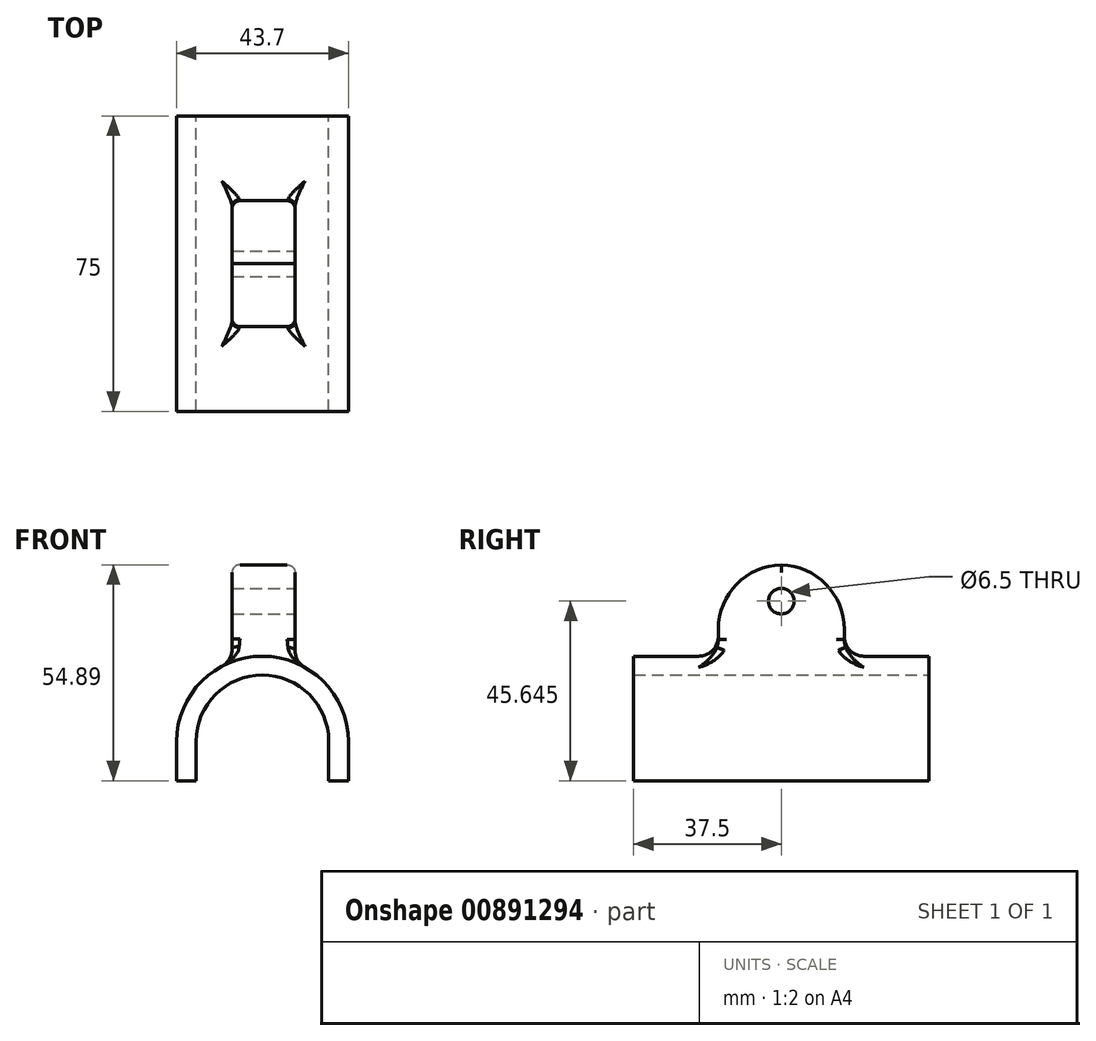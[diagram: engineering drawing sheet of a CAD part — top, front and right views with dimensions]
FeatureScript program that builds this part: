
annotation { "Feature Type Name" : "Feature", "Feature Type Description" : "" }
export const myFeature = defineFeature(function(context is Context, id is Id, definition is map)
    precondition{}
    {
        {
            var Q0;
            Q0=qCreatedBy(makeId("Front.planeOp"),FACE);
            var sketch = newSketch(context, id + "F0", { "sketchPlane" : qUnion([Q0])});
            skArc(sketch, "E0", {"start": v(16.56, 0) * mm, "mid": v(-0.29, 16.85) * mm, "end": v(-17.14, 0) * mm});
            skLineSegment(sketch, "E1", {"start": v(-17.14, 0) * mm, "end": v(-22.14, 0) * mm});
            skLineSegment(sketch, "E2", {"start": v(16.56, 0) * mm, "end": v(21.56, 0) * mm});
            skArc(sketch, "E3", {"start": v(21.56, 0) * mm, "mid": v(-0.29, 21.66) * mm, "end": v(-22.14, 0) * mm});
            skSolve(sketch);
        }
        {
            var Q0;
            Q0=makeQuery(id+"F0.imprint","IMPRINT",FACE,{"disambiguationData":[TD([[makeQuery(id+"F0.imprint","IMPRINT",EDGE,{"derivedFrom":sQuery(id+"F0.wireOp",EDGE,"E0")}),-1.0]])]});
            extrude(context, id + "F1", {"entities" : qUnion([Q0]), "endBound" : BoundingType.SYMMETRIC, "depth" : 75 * mm, "offsetDistance" : 25 * mm});
        }
        {
            var Q0;
            Q0=qCreatedBy(makeId("Top.planeOp"),FACE);
            cPlane(context, id + "F2", {"entities" : qUnion([Q0]), "cplaneType" : CPlaneType.OFFSET, "offset" : 19.9 * mm, "width" : 150 * mm, "height" : 150 * mm});
        }
        {
            var Q0;
            Q0=qCreatedBy(id+"F2.planeOp",FACE);
            var sketch = newSketch(context, id + "F3", { "sketchPlane" : qUnion([Q0])});
            skLineSegment(sketch, "E4.bottom", {"start": v(-8, 16) * mm, "end": v(8, 16) * mm});
            skLineSegment(sketch, "E4.top", {"start": v(-8, -16) * mm, "end": v(8, -16) * mm});
            skLineSegment(sketch, "E4.left", {"start": v(-8, 16) * mm, "end": v(-8, -16) * mm});
            skLineSegment(sketch, "E4.right", {"start": v(8, 16) * mm, "end": v(8, -16) * mm});
            skPoint(sketch, "E4.middle", {"position": v(0, 0) * mm});
            skSolve(sketch);
        }
        {
            var Q0;
            Q0 = qSketchRegion(id + "F3", true);
            extrude(context, id + "F4", {"entities" : qUnion([Q0]), "operationType" : NewBodyOperationType.ADD, "depth" : 25 * mm, "offsetDistance" : 25 * mm});
        }
        {
            var Q0;
            Q0=makeQuery(id+"F4.boolean.opBoolean","INTERSECT",EDGE,{"derivedFrom":[makeQuery(id+"F1.opExtrude","SWEPT_FACE",FACE,{"disambiguationData":[OSD([sQuery(id+"F0.wireOp",EDGE,"E3")])]}),makeQuery(id+"F4.opExtrude","SWEPT_FACE",FACE,{"disambiguationData":[OSD([sQuery(id+"F3.wireOp",EDGE,"E4.right")])]})]});
            var Q1;
            Q1=makeQuery(id+"F4.boolean.opBoolean","INTERSECT",EDGE,{"derivedFrom":[makeQuery(id+"F1.opExtrude","SWEPT_FACE",FACE,{"disambiguationData":[OSD([sQuery(id+"F0.wireOp",EDGE,"E3")])]}),makeQuery(id+"F4.opExtrude","SWEPT_FACE",FACE,{"disambiguationData":[OSD([sQuery(id+"F3.wireOp",EDGE,"E4.left")])]})]});
            fillet(context, id + "F5", {"entities" : qUnion([Q0, Q1]), "radius" : 5 * mm, "tangentPropagation" : true, "allowEdgeOverflow" : false});
        }
        {
            var Q0;
            Q0=makeQuery(id+"F4.boolean.opBoolean","INTERSECT",EDGE,{"derivedFrom":[makeQuery(id+"F1.opExtrude","SWEPT_FACE",FACE,{"disambiguationData":[OSD([sQuery(id+"F0.wireOp",EDGE,"E3")])]}),makeQuery(id+"F4.opExtrude","SWEPT_FACE",FACE,{"disambiguationData":[OSD([sQuery(id+"F3.wireOp",EDGE,"E4.top")])]})]});
            var Q1;
            Q1=makeQuery(id+"F4.boolean.opBoolean","INTERSECT",EDGE,{"derivedFrom":[makeQuery(id+"F1.opExtrude","SWEPT_FACE",FACE,{"disambiguationData":[OSD([sQuery(id+"F0.wireOp",EDGE,"E3")])]}),makeQuery(id+"F4.opExtrude","SWEPT_FACE",FACE,{"disambiguationData":[OSD([sQuery(id+"F3.wireOp",EDGE,"E4.bottom")])]})]});
            fillet(context, id + "F6", {"entities" : qUnion([Q0, Q1]), "radius" : 5 * mm, "tangentPropagation" : true, "allowEdgeOverflow" : false});
        }
        {
            var Q0;
            Q0=makeQuery(id+"F4.opExtrude","CAP_EDGE",EDGE,{"disambiguationData":[OSD([sQuery(id+"F3.wireOp",EDGE,"E4.top")])],"isStart":false});
            var Q1;
            Q1=makeQuery(id+"F4.opExtrude","CAP_EDGE",EDGE,{"disambiguationData":[OSD([sQuery(id+"F3.wireOp",EDGE,"E4.bottom")])],"isStart":false});
            fillet(context, id + "F7", {"entities" : qUnion([Q0, Q1]), "radius" : 16.42 * mm, "tangentPropagation" : true, "allowEdgeOverflow" : false});
        }
        {
            var Q0;
            Q0=makeQuery(id+"F4.opExtrude","SWEPT_FACE",FACE,{"disambiguationData":[OSD([sQuery(id+"F3.wireOp",EDGE,"E4.right")])]});
            var sketch = newSketch(context, id + "F8", { "sketchPlane" : qUnion([Q0])});
            skCircle(sketch, "E5", {"center": v(0, 35.64) * mm, "radius": 3.25 * mm});
            skSolve(sketch);
        }
        {
            var Q0;
            Q0 = qSketchRegion(id + "F8", true);
            extrude(context, id + "F9", {"entities" : qUnion([Q0]), "operationType" : NewBodyOperationType.REMOVE, "oppositeDirection" : true, "depth" : 25 * mm, "offsetDistance" : 25 * mm});
        }
        {
            var Q0;
            Q0=makeQuery(id+"F7.opFillet","BLEND_EDGE",EDGE,{"blendedFrom":[makeQuery(id+"F4.opExtrude","CAP_EDGE",EDGE,{"disambiguationData":[OSD([sQuery(id+"F3.wireOp",EDGE,"E4.top")])],"isStart":false}),makeQuery(id+"F4.opExtrude","SWEPT_FACE",FACE,{"disambiguationData":[OSD([sQuery(id+"F3.wireOp",EDGE,"E4.right")])]})],"blendedInto":[makeQuery(id+"F4.opExtrude","SWEPT_FACE",FACE,{"disambiguationData":[OSD([sQuery(id+"F3.wireOp",EDGE,"E4.right")])]})]});
            var Q1;
            Q1=makeQuery(id+"F7.opFillet","BLEND_EDGE",EDGE,{"blendedFrom":[makeQuery(id+"F4.opExtrude","CAP_EDGE",EDGE,{"disambiguationData":[OSD([sQuery(id+"F3.wireOp",EDGE,"E4.bottom")])],"isStart":false}),makeQuery(id+"F4.opExtrude","SWEPT_FACE",FACE,{"disambiguationData":[OSD([sQuery(id+"F3.wireOp",EDGE,"E4.right")])]})],"blendedInto":[makeQuery(id+"F4.opExtrude","SWEPT_FACE",FACE,{"disambiguationData":[OSD([sQuery(id+"F3.wireOp",EDGE,"E4.right")])]})]});
            var Q2;
            Q2=makeQuery(id+"F7.opFillet","BLEND_EDGE",EDGE,{"blendedFrom":[makeQuery(id+"F4.opExtrude","CAP_EDGE",EDGE,{"disambiguationData":[OSD([sQuery(id+"F3.wireOp",EDGE,"E4.bottom")])],"isStart":false}),makeQuery(id+"F4.opExtrude","SWEPT_FACE",FACE,{"disambiguationData":[OSD([sQuery(id+"F3.wireOp",EDGE,"E4.left")])]})],"blendedInto":[makeQuery(id+"F4.opExtrude","SWEPT_FACE",FACE,{"disambiguationData":[OSD([sQuery(id+"F3.wireOp",EDGE,"E4.left")])]})]});
            var Q3;
            Q3=makeQuery(id+"F7.opFillet","BLEND_EDGE",EDGE,{"blendedFrom":[makeQuery(id+"F4.opExtrude","CAP_EDGE",EDGE,{"disambiguationData":[OSD([sQuery(id+"F3.wireOp",EDGE,"E4.top")])],"isStart":false}),makeQuery(id+"F4.opExtrude","SWEPT_FACE",FACE,{"disambiguationData":[OSD([sQuery(id+"F3.wireOp",EDGE,"E4.left")])]})],"blendedInto":[makeQuery(id+"F4.opExtrude","SWEPT_FACE",FACE,{"disambiguationData":[OSD([sQuery(id+"F3.wireOp",EDGE,"E4.left")])]})]});
            fillet(context, id + "F10", {"entities" : qUnion([Q0, Q1, Q2, Q3]), "radius" : 2 * mm, "tangentPropagation" : true, "allowEdgeOverflow" : false});
        }
        {
            var Q0;
            Q0=makeQuery(id+"F1.opExtrude","SWEPT_FACE",FACE,{"disambiguationData":[OSD([sQuery(id+"F0.wireOp",EDGE,"E2")])]});
            var Q1;
            Q1=makeQuery(id+"F1.opExtrude","SWEPT_FACE",FACE,{"disambiguationData":[OSD([sQuery(id+"F0.wireOp",EDGE,"E1")])]});
            extrude(context, id + "F11", {"entities" : qUnion([Q0, Q1]), "operationType" : NewBodyOperationType.ADD, "depth" : 10 * mm, "offsetDistance" : 25 * mm});
        }
    });
